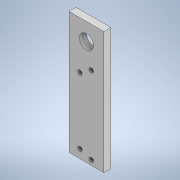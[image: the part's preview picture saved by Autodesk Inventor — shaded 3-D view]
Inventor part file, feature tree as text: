
AUTODESK INVENTOR PART (.ipt)
format: ipt  version: 2020 (Build 240168000, 168)  size: 245,760 bytes
history: native  units: mm
features: sketch x4, extrude x2, hole x2, projected_geometry x2, other x1
ambient origin geometry x8: Origin, YZ Plane, XZ Plane, XY Plane, X Axis, Y Axis, Z Axis, Center Point
bodies: Body1 (feature_tree), Body2 (feature_tree)
feature tree (11):
  other  "솔리드1"
  extrude  "돌출1"  Depth=20.0mm
  hole  "구멍1"  [1 undecoded]
  extrude  "돌출2"  Depth=4.0mm TaperAngle=0.0deg
  hole  "구멍2"  [1 undecoded]
  sketch  "스케치1"
  sketch  "스케치2"
  projected_geometry  "투영된 루프1"
  sketch  "스케치3"
  projected_geometry  "투영된 루프2"
  sketch  "스케치4"
note: 2 required parameter values undecoded (feature->parameter linkage not recoverable at this tier; creation-order binding heuristic only, values carry confidence <= 0.55)
